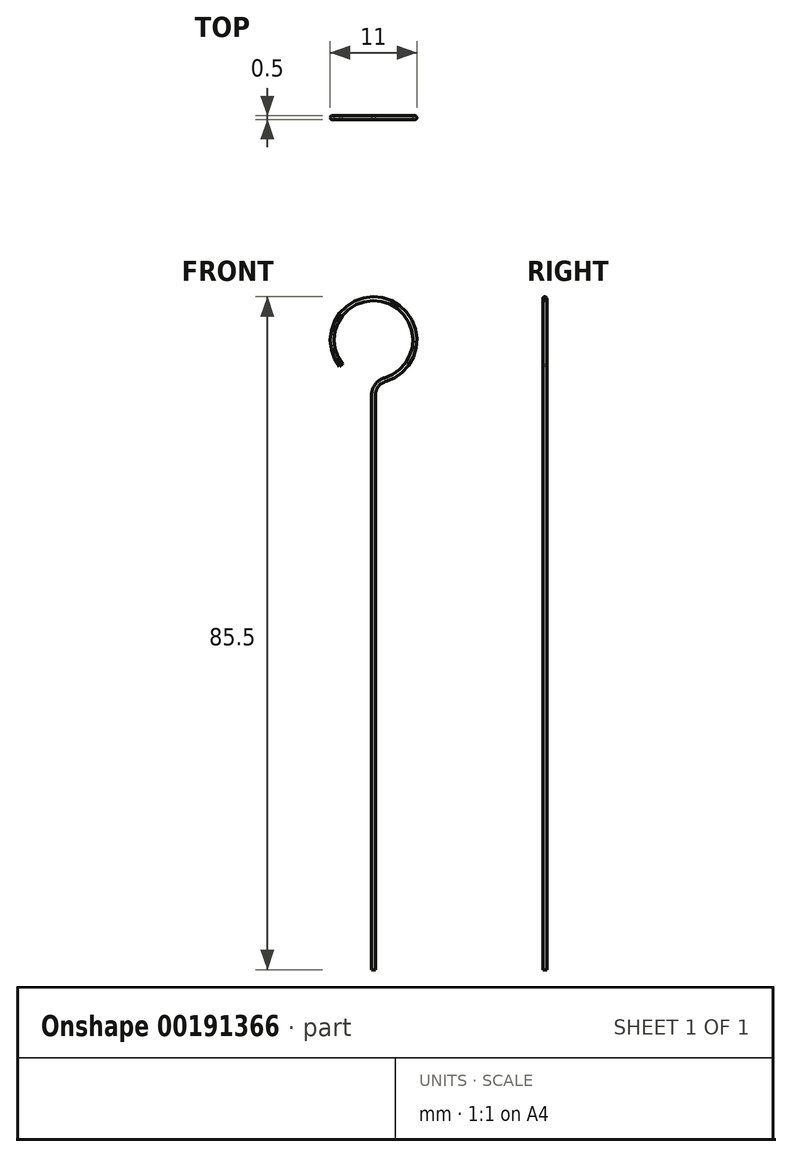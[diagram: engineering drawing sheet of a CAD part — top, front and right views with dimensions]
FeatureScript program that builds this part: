
annotation { "Feature Type Name" : "Feature", "Feature Type Description" : "" }
export const myFeature = defineFeature(function(context is Context, id is Id, definition is map)
    precondition{}
    {
        {
            var Q0;
            Q0=qCreatedBy(makeId("Front.planeOp"),FACE);
            var sketch = newSketch(context, id + "F0", { "sketchPlane" : qUnion([Q0])});
            skArc(sketch, "E0", {"start": v(1.45, -5.05) * mm, "mid": v(1.63, 5) * mm, "end": v(-4.14, -3.22) * mm});
            skLineSegment(sketch, "E1", {"start": v(0, -6.97) * mm, "end": v(0, -80) * mm});
            skPoint(sketch, "E2.visualSharp", {"position": v(0, -5.25) * mm});
            skArc(sketch, "E2.filletArc", {"start": v(1.45, -5.05) * mm, "mid": v(0.4, -5.77) * mm, "end": v(0, -6.97) * mm});
            skSolve(sketch);
        }
        {
            var Q0;
            Q0=sQuery(id+"F0.wireOp",VERTEX,"E1.end");
            var Q1;
            Q1=sQuery(id+"F0.wireOp",EDGE,"E1");
            cPlane(context, id + "F1", {"entities" : qUnion([Q0, Q1]), "cplaneType" : CPlaneType.CURVE_POINT, "offset" : 25 * mm, "width" : 150 * mm, "height" : 150 * mm});
        }
        {
            var Q0;
            Q0=qCreatedBy(id+"F1.planeOp",FACE);
            var sketch = newSketch(context, id + "F2", { "sketchPlane" : qUnion([Q0])});
            skCircle(sketch, "E3", {"center": v(0, 0) * mm, "radius": 0.25 * mm});
            skSolve(sketch);
        }
        {
            var Q0;
            Q0=makeQuery(id+"F2.imprint","IMPRINT",FACE,{"disambiguationData":[TD([[makeQuery(id+"F2.imprint","IMPRINT",EDGE,{"derivedFrom":sQuery(id+"F2.wireOp",EDGE,"E3")}),1.0]])]});
            var Q1;
            Q1=sQuery(id+"F0.wireOp",EDGE,"E1");
            var Q2;
            Q2=sQuery(id+"F0.wireOp",EDGE,"E2.filletArc");
            var Q3;
            Q3=sQuery(id+"F0.wireOp",EDGE,"E0");
            sweep(context, id + "F3", {"profiles" : qUnion([Q0]), "path" : qUnion([Q1, Q2, Q3])});
        }
    });
